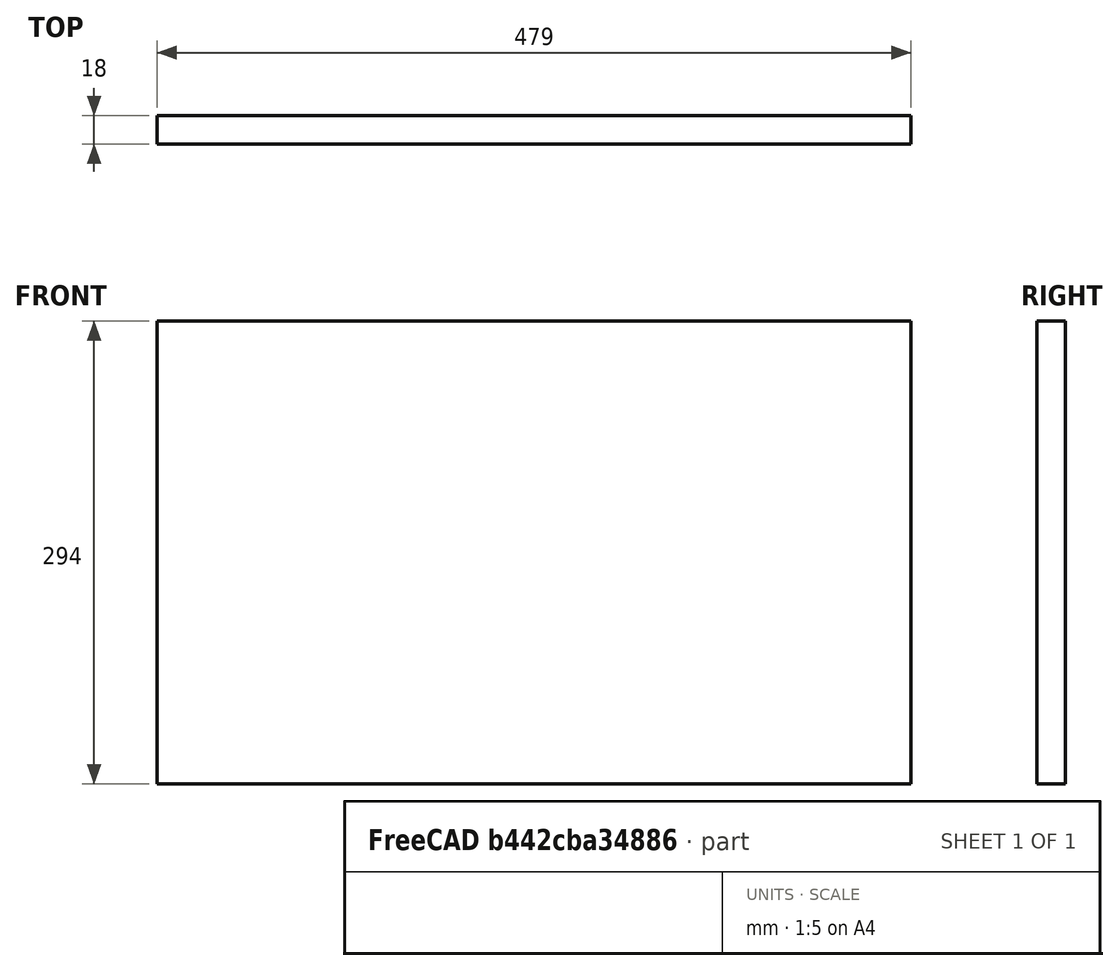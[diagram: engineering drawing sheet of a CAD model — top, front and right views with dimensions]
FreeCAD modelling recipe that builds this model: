
FCSTD DOCUMENT  (FreeCAD 0.17R13541 (Git))
Label: FaceFond
License: All rights reserved
LicenseURL: http://en.wikipedia.org/wiki/All_rights_reserved
objects: Sketcher::SketchObject×1, PartDesign::Pad×1, PartDesign::Body×1
note: 4 computed .brp shape members not serialized (recipe doc carries the construction recipe); baked Part::Feature solids carry a one-line shape summary decoded from their .brp

FEATURE [Sketcher::SketchObject] Sketch
  MapMode = 5
  Placement = pos=(0,0,0) rot=(1,0,0;1.5708rad)
  Support = -> [XZ_Plane]
  sketch-geometry (6):
    g0: LineSegment StartX=-239.5 StartY=147 StartZ=0 EndX=239.5 EndY=147 EndZ=0
    g1: LineSegment StartX=239.5 StartY=147 StartZ=0 EndX=239.5 EndY=-147 EndZ=0
    g2: LineSegment StartX=239.5 StartY=-147 StartZ=0 EndX=-239.5 EndY=-147 EndZ=0
    g3: LineSegment StartX=-239.5 StartY=-147 StartZ=0 EndX=-239.5 EndY=147 EndZ=0
    g4: LineSegment [constr] StartX=-239.5 StartY=147 StartZ=0 EndX=239.5 EndY=-147 EndZ=0
    g5: LineSegment [constr] StartX=-239.5 StartY=-147 StartZ=0 EndX=239.5 EndY=147 EndZ=0
  constraints (16):
    c: Coincident(g0,g1)
    c: Coincident(g1,g2)
    c: Coincident(g2,g3)
    c: Coincident(g3,g0)
    c: Horizontal(g0)
    c: Horizontal(g2)
    c: Vertical(g1)
    c: Vertical(g3)
    c: Coincident(g4,g0)
    c: Coincident(g4,g1)
    c: Coincident(g5,g2)
    c: Coincident(g5,g0)
    c: PointOnObject(g-1,g4)
    c: PointOnObject(g-1,g5)
    c: DistanceX(g0,g0) = 479  'Largeur A'
    c: DistanceY(g1,g1) = 294  'Hauteur C'
FEATURE [PartDesign::Pad] Pad
  Length = 18
  Length2 = 100
  Placement = pos=(0,0,0) rot=(1,0,0;1.5708rad)
  Profile = -> Sketch
  Type = 0
FEATURE [PartDesign::Body] Body  label="Face fond"
  Group = -> [Sketch,Pad]
  Origin = -> Origin
  Tip = -> Pad
